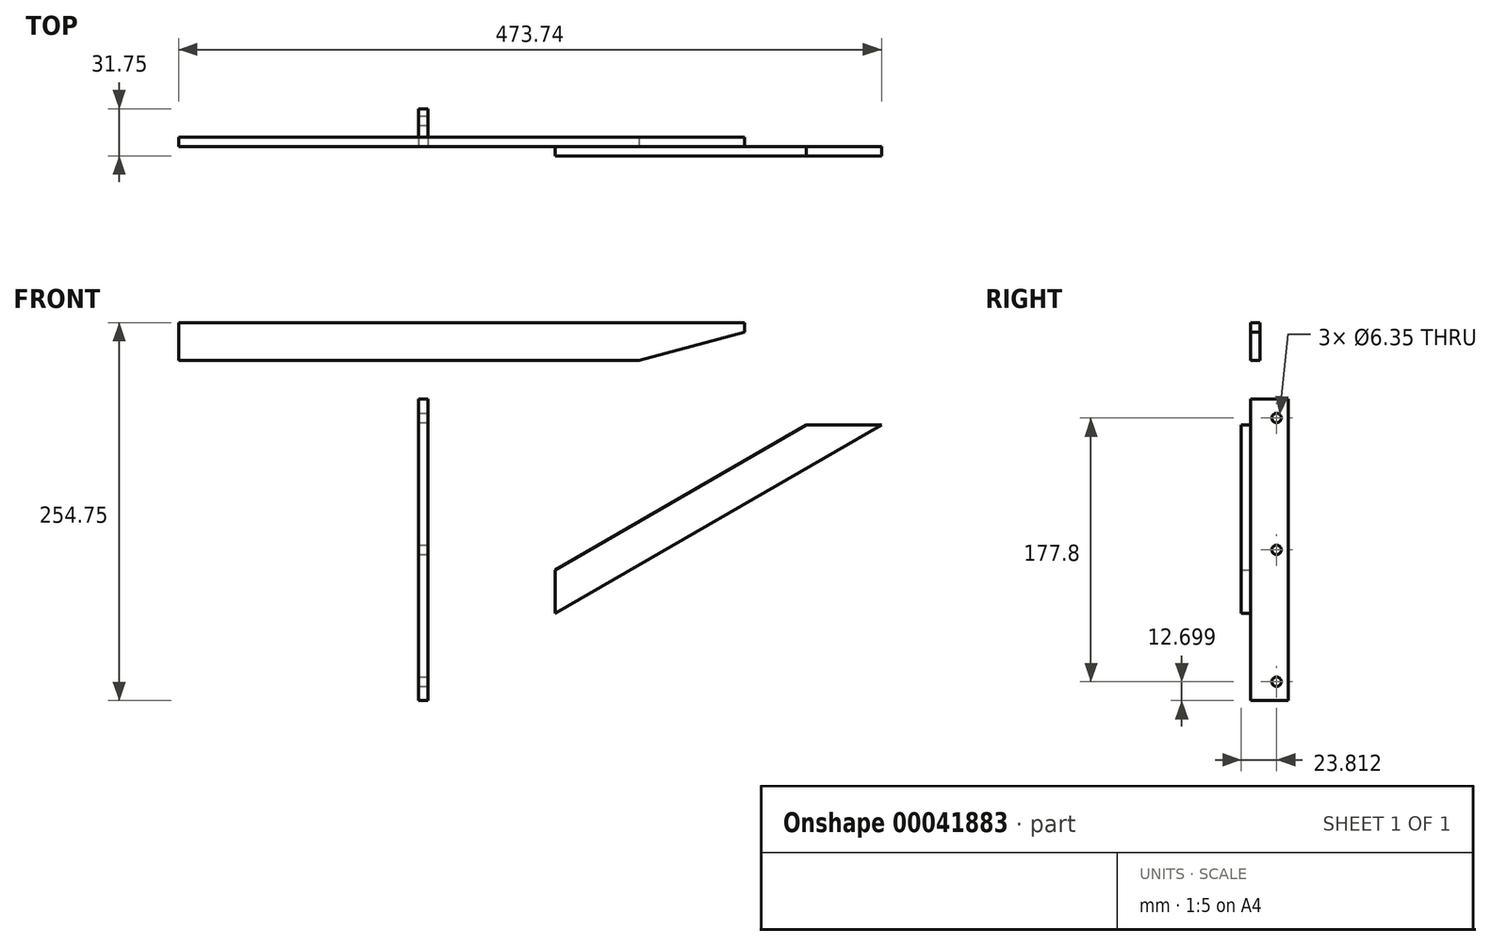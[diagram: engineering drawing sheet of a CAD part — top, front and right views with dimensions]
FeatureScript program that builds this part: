
annotation { "Feature Type Name" : "Feature", "Feature Type Description" : "" }
export const myFeature = defineFeature(function(context is Context, id is Id, definition is map)
    precondition{}
    {
        {
            var Q0;
            Q0=qCreatedBy(makeId("Front.planeOp"),FACE);
            var sketch = newSketch(context, id + "F0", { "sketchPlane" : qUnion([Q0])});
            skLineSegment(sketch, "E0.bottom", {"start": v(-120.88, 167.26) * mm, "end": v(-114.53, 167.26) * mm});
            skLineSegment(sketch, "E0.top", {"start": v(-120.88, -35.94) * mm, "end": v(-114.53, -35.94) * mm});
            skLineSegment(sketch, "E0.left", {"start": v(-120.88, 167.26) * mm, "end": v(-120.88, -35.94) * mm});
            skLineSegment(sketch, "E0.right", {"start": v(-114.53, 167.26) * mm, "end": v(-114.53, -35.94) * mm});
            skSolve(sketch);
        }
        {
            var Q0;
            Q0=qCreatedBy(makeId("Front.planeOp"),FACE);
            var sketch = newSketch(context, id + "F1", { "sketchPlane" : qUnion([Q0])});
            skSolve(sketch);
        }
        {
            var Q0;
            Q0 = qSketchRegion(id + "F1", true);
            var Q1;
            Q1=makeQuery(id+"F0.imprint","IMPRINT",FACE,{"disambiguationData":[TD([[makeQuery(id+"F0.imprint","IMPRINT",EDGE,{"derivedFrom":sQuery(id+"F0.wireOp",EDGE,"E0.bottom")}),-1.0]])]});
            extrude(context, id + "F2", {"entities" : qUnion([Q0, Q1]), "oppositeDirection" : true, "depth" : 25.4 * mm});
        }
        {
            var Q0;
            Q0=makeQuery(id+"F2.opExtrude","SWEPT_FACE",FACE,{"disambiguationData":[OSD([sQuery(id+"F0.wireOp",EDGE,"E0.right")])]});
            var sketch = newSketch(context, id + "F3", { "sketchPlane" : qUnion([Q0])});
            skLineSegment(sketch, "E1", {"start": v(17.46, 167.26) * mm, "end": v(17.46, -35.94) * mm});
            skPoint(sketch, "E2", {"position": v(17.46, 154.56) * mm});
            skPoint(sketch, "E3", {"position": v(17.46, -23.24) * mm});
            skPoint(sketch, "E4", {"position": v(17.46, 65.66) * mm});
            skSolve(sketch);
        }
        {
            var Q0;
            Q0=sQuery(id+"F3.wireOp",VERTEX,"E2");
            var Q1;
            Q1=sQuery(id+"F3.wireOp",VERTEX,"E4");
            var Q2;
            Q2=sQuery(id+"F3.wireOp",VERTEX,"E3");
            var Q3;
            Q3=makeQuery(id+"F2.opExtrude","SWEPT_BODY",BODY,{"disambiguationData":[OSD([sQuery(id+"F0.wireOp",EDGE,"E0.bottom"),sQuery(id+"F0.wireOp",EDGE,"E0.top"),sQuery(id+"F0.wireOp",EDGE,"E0.left"),sQuery(id+"F0.wireOp",EDGE,"E0.right")])]});
            hole(context, id + "F4", {"style" : HoleStyle.SIMPLE, "holeDiameter" : 6.35 * mm, "endStyle" : HoleEndStyle.THROUGH, "locations" : qUnion([Q0, Q1, Q2]), "scope" : qUnion([Q3])});
        }
        {
            var Q0;
            Q0=makeQuery(id+"F2.opExtrude","CAP_FACE",FACE,{"disambiguationData":[OSD([sQuery(id+"F0.wireOp",EDGE,"E0.bottom"),sQuery(id+"F0.wireOp",EDGE,"E0.top"),sQuery(id+"F0.wireOp",EDGE,"E0.left"),sQuery(id+"F0.wireOp",EDGE,"E0.right")])],"isStart":true});
            var sketch = newSketch(context, id + "F5", { "sketchPlane" : qUnion([Q0])});
            skLineSegment(sketch, "E5.bottom", {"start": v(-282.65, 218.81) * mm, "end": v(98.86, 218.81) * mm});
            skLineSegment(sketch, "E5.top", {"start": v(-282.65, 193.41) * mm, "end": v(27.76, 193.41) * mm});
            skLineSegment(sketch, "E5.left", {"start": v(-282.65, 218.81) * mm, "end": v(-282.65, 193.41) * mm});
            skLineSegment(sketch, "E5.right", {"start": v(98.86, 218.81) * mm, "end": v(98.86, 212.46) * mm});
            skLineSegment(sketch, "E6", {"start": v(98.86, 212.46) * mm, "end": v(27.76, 193.41) * mm});
            skSolve(sketch);
        }
        {
            var Q0;
            Q0 = qSketchRegion(id + "F5", true);
            extrude(context, id + "F6", {"entities" : qUnion([Q0]), "oppositeDirection" : true, "depth" : 6.35 * mm});
        }
        {
            var Q0;
            Q0=makeQuery(id+"F2.opExtrude","CAP_FACE",FACE,{"disambiguationData":[OSD([sQuery(id+"F0.wireOp",EDGE,"E0.bottom"),sQuery(id+"F0.wireOp",EDGE,"E0.top"),sQuery(id+"F0.wireOp",EDGE,"E0.left"),sQuery(id+"F0.wireOp",EDGE,"E0.right")])],"isStart":true});
            var sketch = newSketch(context, id + "F7", { "sketchPlane" : qUnion([Q0])});
            skLineSegment(sketch, "E7", {"start": v(-28.88, 52.17) * mm, "end": v(-28.88, 22.84) * mm});
            skLineSegment(sketch, "E8", {"start": v(140.3, 149.84) * mm, "end": v(148.71, 149.84) * mm});
            skLineSegment(sketch, "E9", {"start": v(148.71, 149.84) * mm, "end": v(191.1, 149.84) * mm});
            skLineSegment(sketch, "E10", {"start": v(-28.88, 22.84) * mm, "end": v(191.1, 149.84) * mm});
            skLineSegment(sketch, "E11.0", {"start": v(-28.88, 52.17) * mm, "end": v(140.3, 149.84) * mm});
            skSolve(sketch);
        }
        {
            var Q0;
            Q0 = qSketchRegion(id + "F7", true);
            extrude(context, id + "F8", {"entities" : qUnion([Q0]), "depth" : 6.35 * mm});
        }
    });
